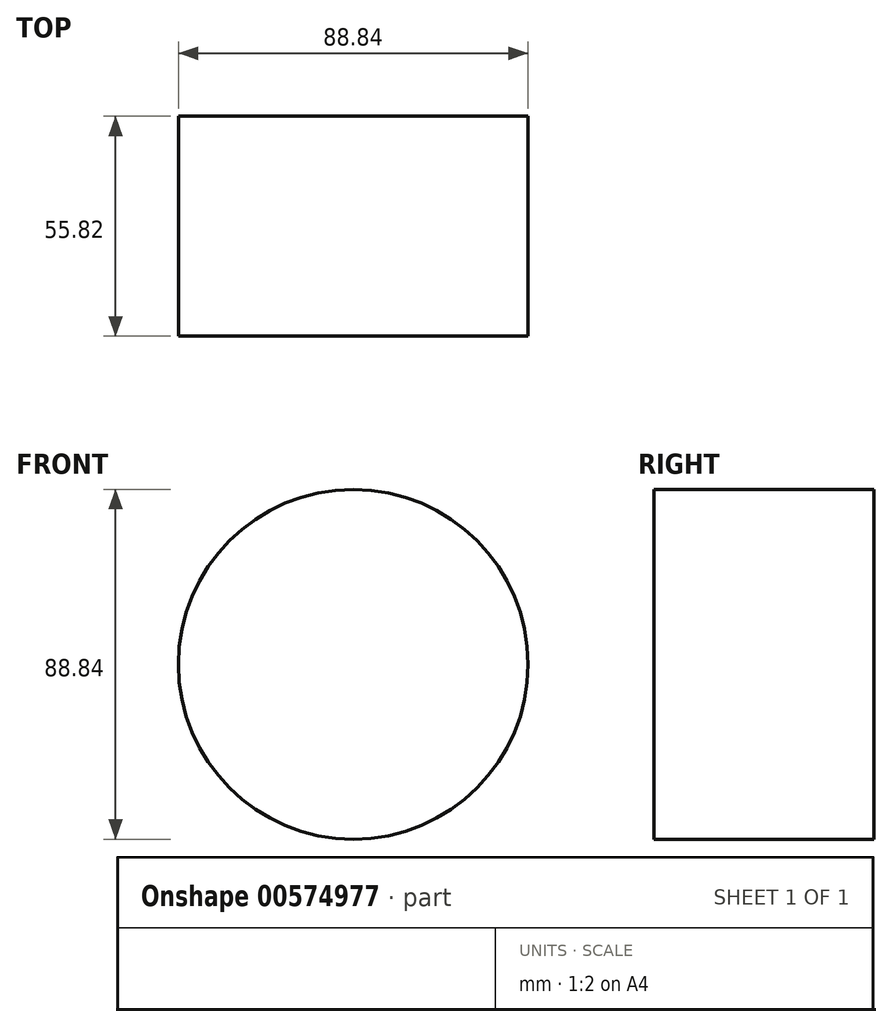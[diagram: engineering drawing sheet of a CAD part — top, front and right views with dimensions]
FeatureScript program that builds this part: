
annotation { "Feature Type Name" : "Feature", "Feature Type Description" : "" }
export const myFeature = defineFeature(function(context is Context, id is Id, definition is map)
    precondition{}
    {
        {
            var Q0;
            Q0=qCreatedBy(makeId("Top.planeOp"),FACE);
            var sketch = newSketch(context, id + "F0", { "sketchPlane" : qUnion([Q0])});
            skLineSegment(sketch, "E0.bottom", {"start": v(44.42, -27.91) * mm, "end": v(-44.42, -27.91) * mm});
            skLineSegment(sketch, "E0.top", {"start": v(44.42, 27.91) * mm, "end": v(-44.42, 27.91) * mm});
            skLineSegment(sketch, "E0.left", {"start": v(44.42, -27.91) * mm, "end": v(44.42, 27.91) * mm});
            skLineSegment(sketch, "E0.right", {"start": v(-44.42, -27.91) * mm, "end": v(-44.42, 27.91) * mm});
            skPoint(sketch, "E0.middle", {"position": v(0, 0) * mm});
            skLineSegment(sketch, "E1", {"start": v(0, 27.91) * mm, "end": v(0, -27.91) * mm});
            skSolve(sketch);
        }
        {
            var Q0;
            {var subQ0=sQuery(id+"F0.wireOp",EDGE,"E0.right");Q0=makeQuery(id+"F0.imprint","IMPRINT",FACE,{"disambiguationData":[TD([[makeQuery(id+"F0.imprint","IMPRINT",EDGE,{"derivedFrom":subQ0}),-1.0]])]});}
            var Q1;
            Q1=sQuery(id+"F0.wireOp",EDGE,"E1");
            revolve(context, id + "F1", {"entities" : qUnion([Q0]), "axis" : qUnion([Q1]), "revolveType" : RevolveType.FULL});
        }
    });
